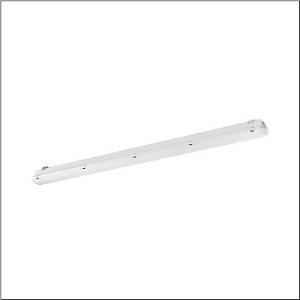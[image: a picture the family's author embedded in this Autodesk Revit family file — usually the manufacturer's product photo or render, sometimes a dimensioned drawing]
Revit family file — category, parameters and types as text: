
# Revit family: monsun_r__11xtreme_mo_51fe10dp440m_4875
name_source: partatom
category: Lighting Fixtures
units: mm (PartAtom-declared; Revit-internal decimal feet)

## family parameters
Cut with Voids When Loaded = No
Host = Face
Light Source = No
Part Type = Normal
Room Calculation Point = No
Round Connector Dimension = Use Diameter
Shared = No

## types (1)
- --- (1 x LED, 4200 lm, 22.3 W, 4000K)
    Apparent Load = 22 VA
    CIE Flux Codes = 47 77 93 94 100
    Color Rendering = 80
    Color Temperature = 4000K
    Default Elevation = 1800 mm
    Description = Monsun® 11Xtreme MO, damp-proof luminaire, chain hanger, primary optical cover: enclosure, of PMMA, light emission: direct distribution, primary light characteristic: symmetric, installation type: suspended mounting, surface-mounted, horizontal mounting, vertical mounting, LED, rated luminous flux: 4.200lm, luminous efficacy: 188lm/W, light colour: 840, colour temperature: 4000K, control gear: DALI 2, with terminal, 5-pole, max. 2.5mm², mains connection: 220..240V, AC, 50/60Hz, rated input power: 22W, luminaire housing, of glass-fibre reinforced polyester, uncoated, bright grey, incl. chain hanger, length: 1.590mm, width: 90mm, height: 88mm, clip for enclosure, of stainless steel (V2A), ceiling mounting element, of stainless steel (V2A), chain hanger, of stainless steel (V2A), protection rating (complete): IP66, insulation class (complete): insulation class I (protective earthing), certification: CE, ENEC, VDE, UKCA, protection symbol: D, impact resistance: IK04, permissible operating ambient temperature: -25..+50°C, standard: EN 50419, EN 60598-2-1, corresponds to IFS (International Featured Standards) requirements for safety and quality in the food industry, for indoor or canopied outdoor use, no direct snow, no direct sun, no direct rain, LABS conformity tested according to VDMA 24364:2018-05, contact your sales advisor before using the luminaires in applications with unclear chemical exposure, large temperature fluctuations or condensation-forming humidity, packaging unit: 1 piece
    Height = 88 mm
    Lamp = 1 x LED
    Lamp Light Flux = 4200 lm
    Lamp Power = 22.3 W
    Lamp count = 1
    Length = 1590 mm
    Luminous efficacy = 188 lm/W
    Manufacturer = Siteco
    ModVariant = No
    Model = 51FE10DP440M
    Mounting Place = Ceiling
    Mounting Type = Surface mounted
    Number of Poles = 1
    OnlyDefault = Yes
    Power Factor = 1
    Product Name = Monsun® 11Xtreme MO
    Product group = damp-proof luminaire
    ProductGroupID = 300
    Protection Class = Protection class I
    Protection Degree = IP 66
    RLX_Detail_Level = 1
    RLX_Emergency_Light_Flux = 0 lm
    RLX_Emergency_Type = 0
    RLX_Emergency_Type_DB = No
    RlxData = <blob elided: 87573 chars, md5=525480e0>
    Socket = socket
    Standby Power = 0 W
    System Light Flux = 4200 lm
    System Power = 22 W
    Type Comments = factory setting: luminous flux: 100 % | dim-lin: 254 | 149 mA
    Type Image = l_1349234.jpg
    URL = http://relux.com
    VarID = @adj_017712
    Voltage = 0 V
    Weight = 0.00 kg
    Width = 90 mm

## geometry (parser evidence)
native form markers: Blend x4, Sweep x13
no freeform markers — native parametric forms only
